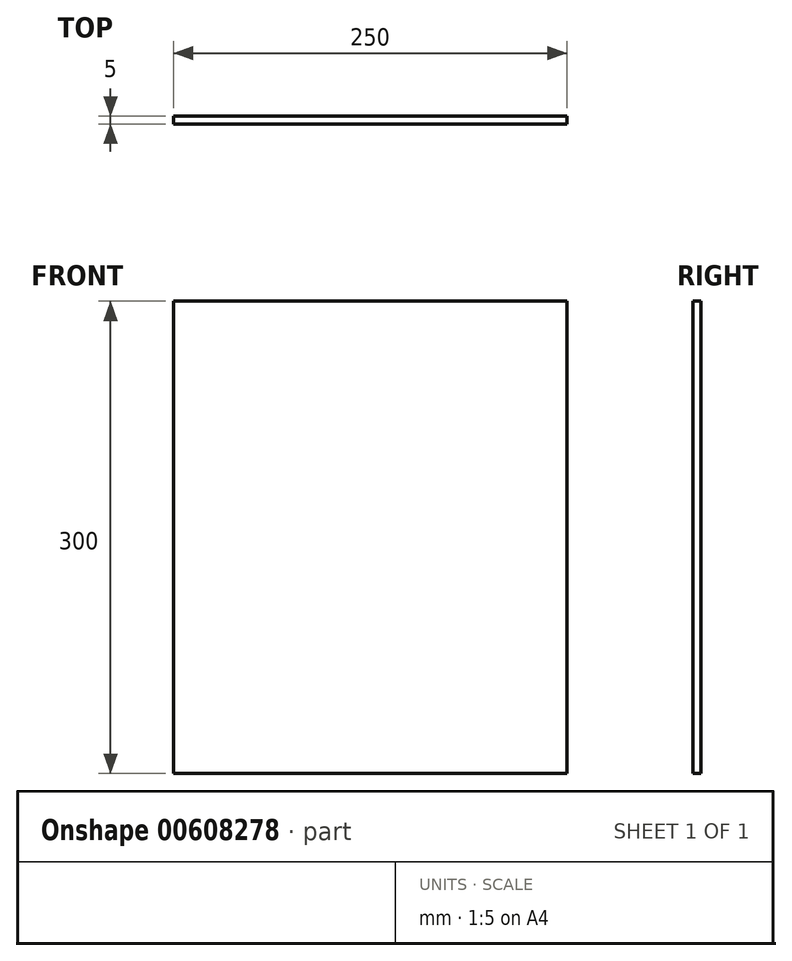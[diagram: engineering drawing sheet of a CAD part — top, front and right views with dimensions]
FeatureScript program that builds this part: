
annotation { "Feature Type Name" : "Feature", "Feature Type Description" : "" }
export const myFeature = defineFeature(function(context is Context, id is Id, definition is map)
    precondition{}
    {
        {
            var Q0;
            Q0=qCreatedBy(makeId("Front.planeOp"),FACE);
            var sketch = newSketch(context, id + "F0", { "sketchPlane" : qUnion([Q0])});
            skLineSegment(sketch, "E0.bottom", {"start": v(-125, 150) * mm, "end": v(125, 150) * mm});
            skLineSegment(sketch, "E0.top", {"start": v(-125, -150) * mm, "end": v(125, -150) * mm});
            skLineSegment(sketch, "E0.left", {"start": v(-125, 150) * mm, "end": v(-125, -150) * mm});
            skLineSegment(sketch, "E0.right", {"start": v(125, 150) * mm, "end": v(125, -150) * mm});
            skPoint(sketch, "E0.middle", {"position": v(0, 0) * mm});
            skSolve(sketch);
        }
        {
            var Q0;
            Q0 = qSketchRegion(id + "F0", true);
            extrude(context, id + "F1", {"entities" : qUnion([Q0]), "depth" : 5 * mm, "offsetDistance" : 25 * mm});
        }
    });
